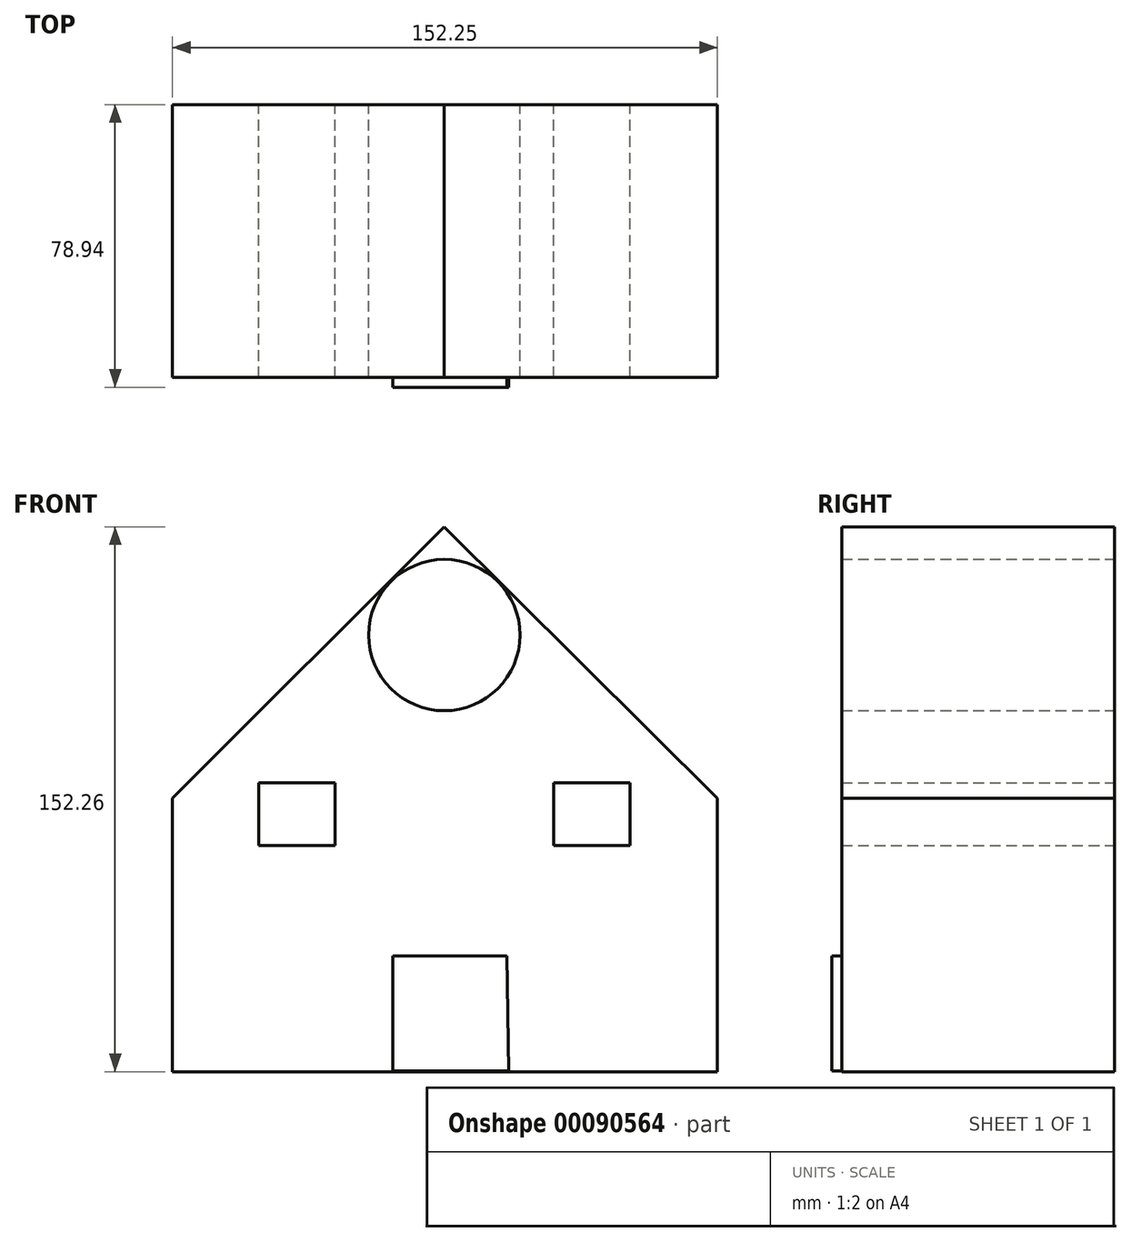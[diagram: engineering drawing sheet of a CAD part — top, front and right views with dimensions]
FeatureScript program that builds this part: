
annotation { "Feature Type Name" : "Feature", "Feature Type Description" : "" }
export const myFeature = defineFeature(function(context is Context, id is Id, definition is map)
    precondition{}
    {
        {
            var Q0;
            Q0=qCreatedBy(makeId("Front.planeOp"),FACE);
            var sketch = newSketch(context, id + "F0", { "sketchPlane" : qUnion([Q0])});
            skLineSegment(sketch, "E0", {"start": v(0, 75.88) * mm, "end": v(-75.96, 0) * mm});
            skLineSegment(sketch, "E1", {"start": v(-75.96, 0) * mm, "end": v(-75.96, -76.38) * mm});
            skLineSegment(sketch, "E2", {"start": v(-75.96, -76.38) * mm, "end": v(76.3, -76.38) * mm});
            skLineSegment(sketch, "E3", {"start": v(76.3, -76.38) * mm, "end": v(76.3, 0) * mm});
            skLineSegment(sketch, "E4", {"start": v(76.3, 0) * mm, "end": v(0, 75.88) * mm});
            skSolve(sketch);
        }
        {
            var Q0;
            Q0 = qSketchRegion(id + "F0", true);
            extrude(context, id + "F1", {"entities" : qUnion([Q0]), "depth" : 76.2 * mm});
        }
        {
            var Q0;
            Q0=qCreatedBy(makeId("Front.planeOp"),FACE);
            var sketch = newSketch(context, id + "F2", { "sketchPlane" : qUnion([Q0])});
            skLineSegment(sketch, "E5", {"start": v(17.5, -44) * mm, "end": v(-14.37, -44) * mm});
            skLineSegment(sketch, "E6", {"start": v(-14.37, -44) * mm, "end": v(-14.37, -76.21) * mm});
            skLineSegment(sketch, "E7", {"start": v(-14.37, -76.21) * mm, "end": v(18, -76.21) * mm});
            skLineSegment(sketch, "E8", {"start": v(18, -76.21) * mm, "end": v(17.5, -44) * mm});
            skSolve(sketch);
        }
        {
            var Q0;
            Q0 = qSketchRegion(id + "F2", true);
            extrude(context, id + "F3", {"entities" : qUnion([Q0]), "operationType" : NewBodyOperationType.ADD, "depth" : 78.94 * mm});
        }
        {
            var Q0;
            Q0=qCreatedBy(makeId("Front.planeOp"),FACE);
            var sketch = newSketch(context, id + "F4", { "sketchPlane" : qUnion([Q0])});
            skLineSegment(sketch, "E9.bottom", {"start": v(-51.87, 4.3) * mm, "end": v(-30.54, 4.3) * mm});
            skLineSegment(sketch, "E9.top", {"start": v(-51.87, -13.23) * mm, "end": v(-30.54, -13.23) * mm});
            skLineSegment(sketch, "E9.left", {"start": v(-51.87, 4.3) * mm, "end": v(-51.87, -13.23) * mm});
            skLineSegment(sketch, "E9.right", {"start": v(-30.54, 4.3) * mm, "end": v(-30.54, -13.23) * mm});
            skLineSegment(sketch, "E10", {"start": v(-41.2, 4.3) * mm, "end": v(-41.2, -13.23) * mm});
            skLineSegment(sketch, "E11", {"start": v(-51.87, -4.47) * mm, "end": v(-30.54, -4.47) * mm});
            skLineSegment(sketch, "E12.MirrorCS", {"start": v(51.87, 4.3) * mm, "end": v(51.87, -13.23) * mm});
            skLineSegment(sketch, "E13.MirrorCS", {"start": v(41.2, 4.3) * mm, "end": v(41.2, -13.23) * mm});
            skLineSegment(sketch, "E14.MirrorCS", {"start": v(51.87, -4.47) * mm, "end": v(30.54, -4.47) * mm});
            skLineSegment(sketch, "E15.MirrorCS", {"start": v(30.54, 4.3) * mm, "end": v(30.54, -13.23) * mm});
            skLineSegment(sketch, "E16.MirrorCS", {"start": v(51.87, 4.3) * mm, "end": v(30.54, 4.3) * mm});
            skLineSegment(sketch, "E17.MirrorCS", {"start": v(51.87, -13.23) * mm, "end": v(30.54, -13.23) * mm});
            skSolve(sketch);
        }
        {
            var Q0;
            Q0 = qSketchRegion(id + "F4", true);
            extrude(context, id + "F5", {"entities" : qUnion([Q0]), "operationType" : NewBodyOperationType.REMOVE, "depth" : 80.46 * mm});
        }
        {
            var Q0;
            Q0=qCreatedBy(makeId("Front.planeOp"),FACE);
            var sketch = newSketch(context, id + "F6", { "sketchPlane" : qUnion([Q0])});
            skCircle(sketch, "E18", {"center": v(0, 45.63) * mm, "radius": 21.14 * mm});
            skSolve(sketch);
        }
        {
            var Q0;
            Q0 = qSketchRegion(id + "F6", true);
            extrude(context, id + "F7", {"entities" : qUnion([Q0]), "operationType" : NewBodyOperationType.REMOVE, "depth" : 84.05 * mm});
        }
    });
